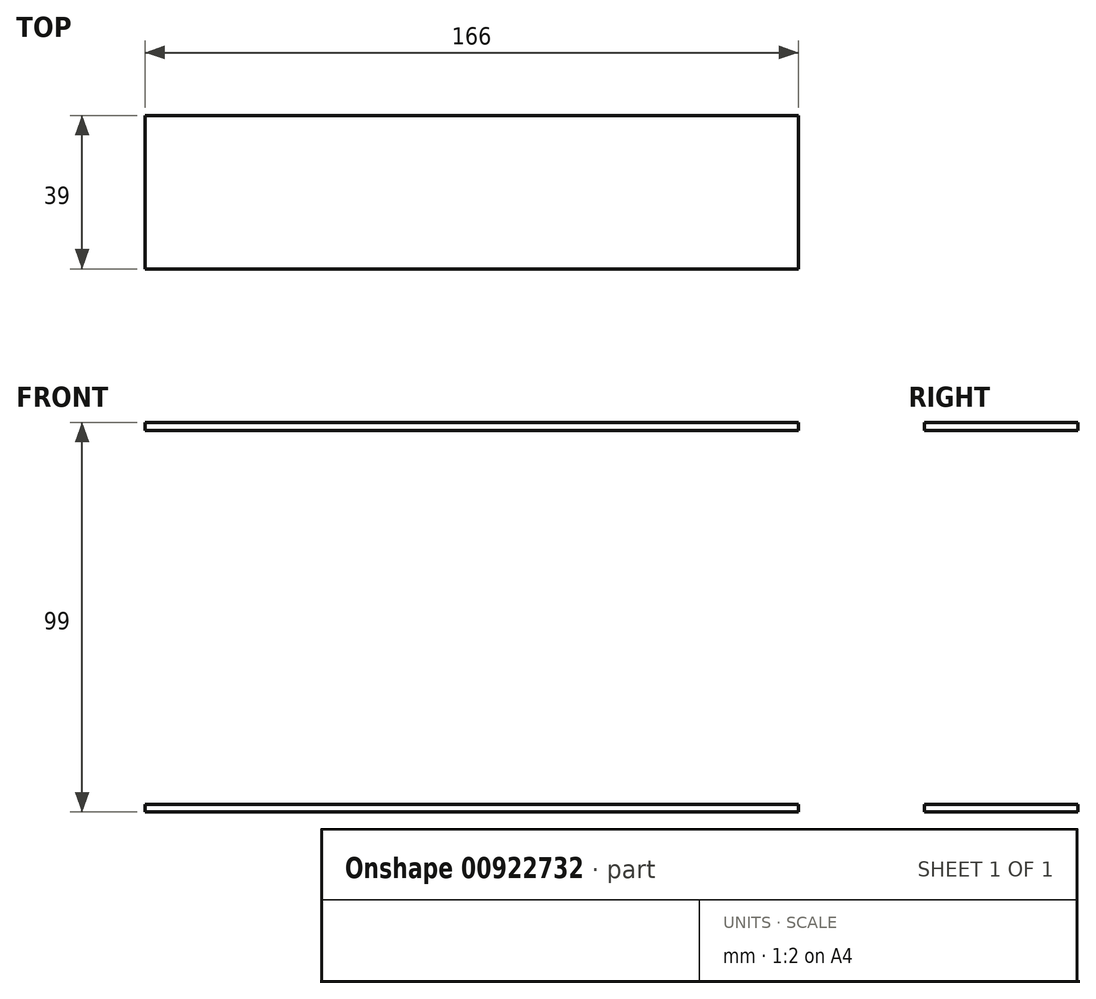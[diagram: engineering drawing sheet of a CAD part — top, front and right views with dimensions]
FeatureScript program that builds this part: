
annotation { "Feature Type Name" : "Feature", "Feature Type Description" : "" }
export const myFeature = defineFeature(function(context is Context, id is Id, definition is map)
    precondition{}
    {
        {
            var Q0;
            Q0=qCreatedBy(makeId("Top.planeOp"),FACE);
            var sketch = newSketch(context, id + "F0", { "sketchPlane" : qUnion([Q0])});
            skLineSegment(sketch, "E0.bottom", {"start": v(83, -19.5) * mm, "end": v(-83, -19.5) * mm});
            skLineSegment(sketch, "E0.top", {"start": v(83, 19.5) * mm, "end": v(-83, 19.5) * mm});
            skLineSegment(sketch, "E0.left", {"start": v(83, -19.5) * mm, "end": v(83, 19.5) * mm});
            skLineSegment(sketch, "E0.right", {"start": v(-83, -19.5) * mm, "end": v(-83, 19.5) * mm});
            skPoint(sketch, "E0.middle", {"position": v(0, 0) * mm});
            skSolve(sketch);
        }
        {
            var Q0;
            Q0 = qSketchRegion(id + "F0", true);
            extrude(context, id + "F1", {"entities" : qUnion([Q0]), "endBound" : BoundingType.SYMMETRIC, "depth" : 2 * mm, "offsetDistance" : 25 * mm});
        }
        {
            var Q0;
            Q0=makeQuery(id+"F1.opExtrude","SWEPT_BODY",BODY,{"disambiguationData":[OSD([sQuery(id+"F0.wireOp",EDGE,"E0.bottom"),sQuery(id+"F0.wireOp",EDGE,"E0.top"),sQuery(id+"F0.wireOp",EDGE,"E0.left"),sQuery(id+"F0.wireOp",EDGE,"E0.right")])]});
            transform(context, id + "F2", {"entities" : qUnion([Q0]), "transformType" : TransformType.TRANSLATION_3D, "dx" : 0 * mm, "dy" : 0 * mm, "dz" : -97 * mm, "makeCopy" : true});
        }
    });
